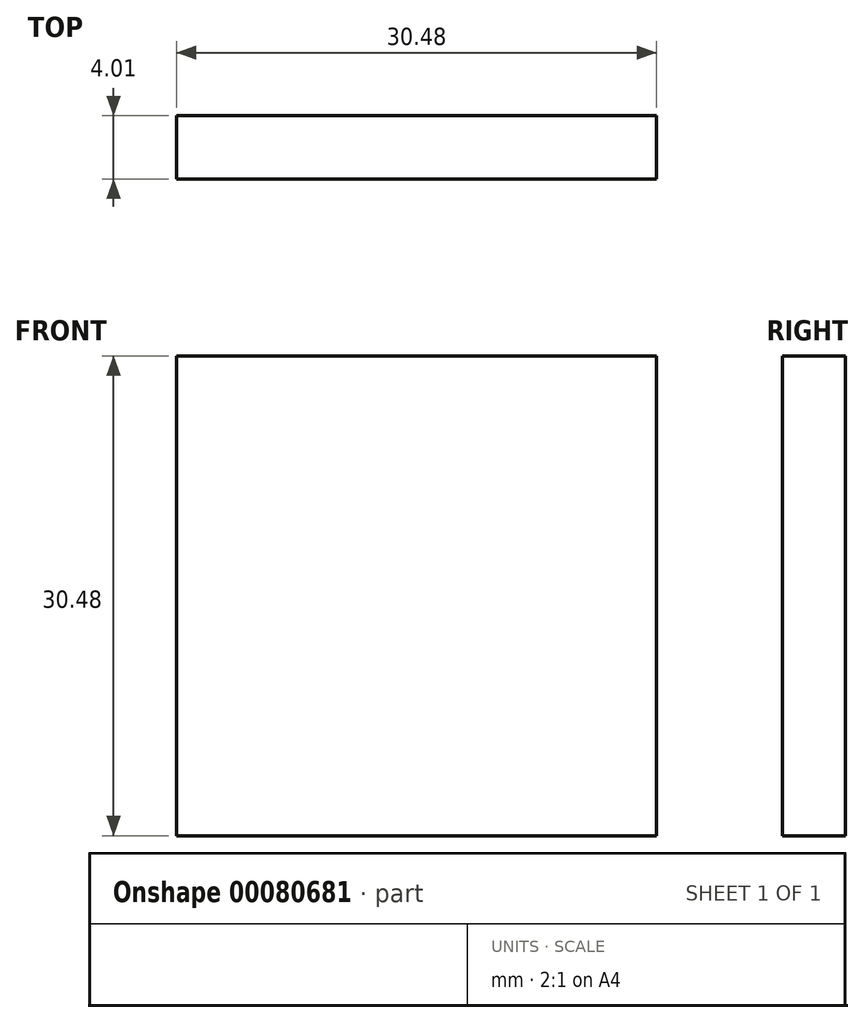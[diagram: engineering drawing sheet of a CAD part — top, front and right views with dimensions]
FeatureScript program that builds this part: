
annotation { "Feature Type Name" : "Feature", "Feature Type Description" : "" }
export const myFeature = defineFeature(function(context is Context, id is Id, definition is map)
    precondition{}
    {
        {
            var Q0;
            Q0=qCreatedBy(makeId("Front.planeOp"),FACE);
            var sketch = newSketch(context, id + "F0", { "sketchPlane" : qUnion([Q0])});
            skLineSegment(sketch, "E0.bottom", {"start": v(-15.24, 15.24) * mm, "end": v(15.24, 15.24) * mm});
            skLineSegment(sketch, "E0.top", {"start": v(-15.24, -15.24) * mm, "end": v(15.24, -15.24) * mm});
            skLineSegment(sketch, "E0.left", {"start": v(-15.24, 15.24) * mm, "end": v(-15.24, -15.24) * mm});
            skLineSegment(sketch, "E0.right", {"start": v(15.24, 15.24) * mm, "end": v(15.24, -15.24) * mm});
            skPoint(sketch, "E0.middle", {"position": v(0, 0) * mm});
            skSolve(sketch);
        }
        {
            var Q0;
            Q0=makeQuery(id+"F0.imprint","IMPRINT",FACE,{"disambiguationData":[TD([[makeQuery(id+"F0.imprint","IMPRINT",EDGE,{"derivedFrom":sQuery(id+"F0.wireOp",EDGE,"E0.bottom")}),-1.0]])]});
            extrude(context, id + "F1", {"entities" : qUnion([Q0]), "depth" : 4 * mm});
        }
    });
